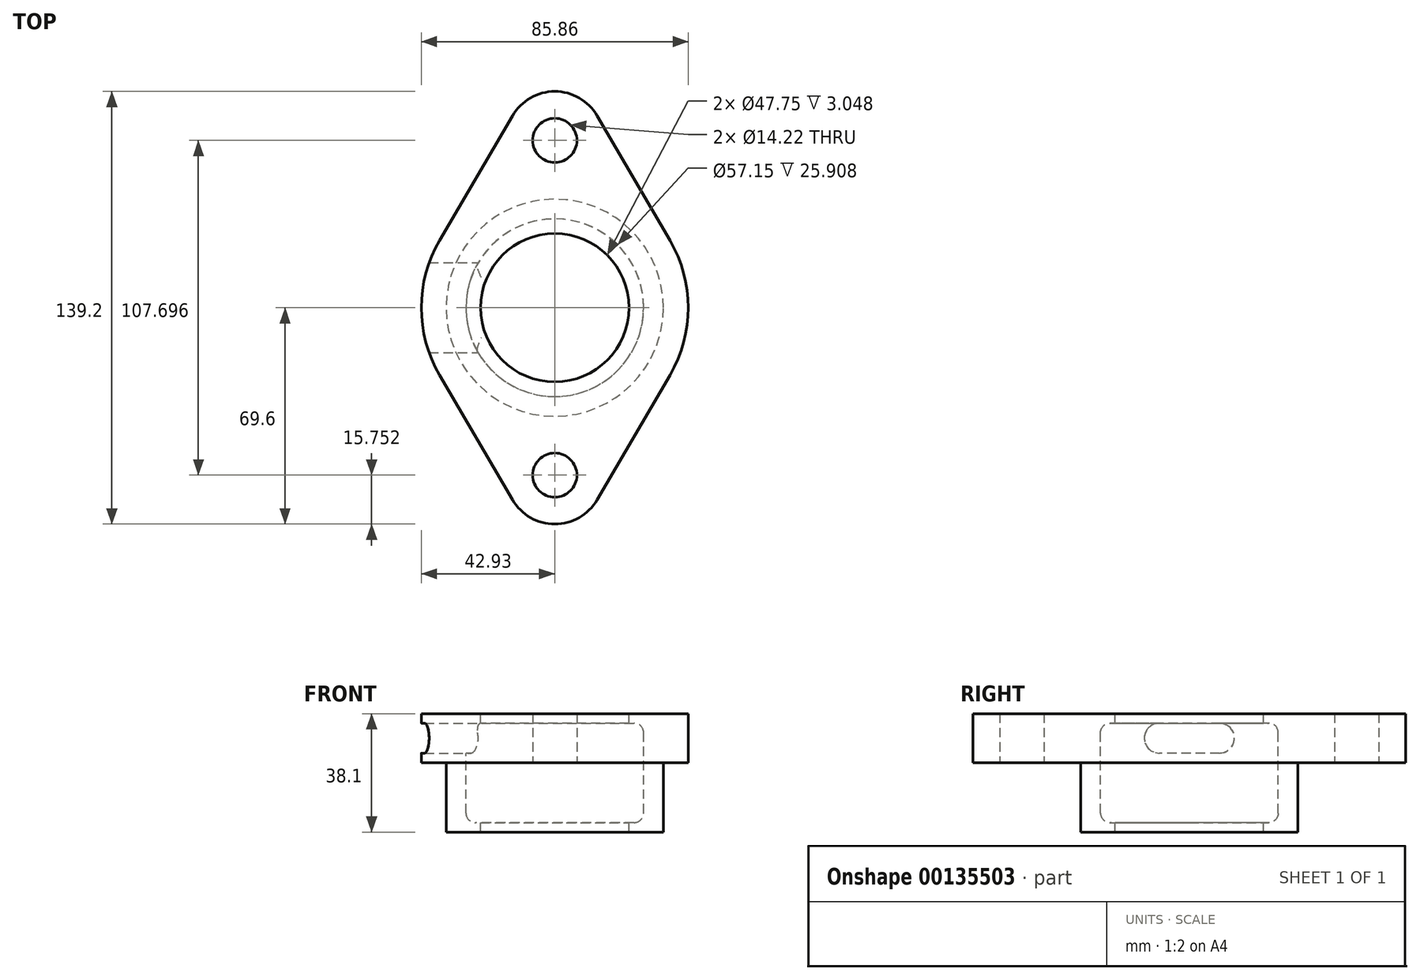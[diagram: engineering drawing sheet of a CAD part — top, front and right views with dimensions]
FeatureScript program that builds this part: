
annotation { "Feature Type Name" : "Feature", "Feature Type Description" : "" }
export const myFeature = defineFeature(function(context is Context, id is Id, definition is map)
    precondition{}
    {
        {
            var Q0;
            Q0=qCreatedBy(makeId("Top.planeOp"),FACE);
            var sketch = newSketch(context, id + "F0", { "sketchPlane" : qUnion([Q0])});
            skArc(sketch, "E0", {"start": v(-37.06, 21.67) * mm, "mid": v(-42.93, 0) * mm, "end": v(-37.06, -21.67) * mm});
            skLineSegment(sketch, "E1", {"start": v(0, 0) * mm, "end": v(0, 53.85) * mm, "construction": true});
            skLineSegment(sketch, "E2", {"start": v(0, 0) * mm, "end": v(0, -53.85) * mm, "construction": true});
            skCircle(sketch, "E3", {"center": v(0, 53.85) * mm, "radius": 7.11 * mm});
            skCircle(sketch, "E4", {"center": v(0, -53.85) * mm, "radius": 7.11 * mm});
            skArc(sketch, "E5", {"start": v(13.6, 61.8) * mm, "mid": v(0, 69.6) * mm, "end": v(-13.6, 61.8) * mm});
            skArc(sketch, "E6", {"start": v(-13.6, -61.8) * mm, "mid": v(0, -69.6) * mm, "end": v(13.6, -61.8) * mm});
            skLineSegment(sketch, "E7", {"start": v(-37.06, 21.67) * mm, "end": v(-13.6, 61.8) * mm});
            skLineSegment(sketch, "E8", {"start": v(13.6, 61.8) * mm, "end": v(37.06, 21.67) * mm});
            skLineSegment(sketch, "E9", {"start": v(37.06, -21.67) * mm, "end": v(13.6, -61.8) * mm});
            skLineSegment(sketch, "E10", {"start": v(-13.6, -61.8) * mm, "end": v(-37.06, -21.67) * mm});
            skArc(sketch, "E11.trimOffspring", {"start": v(37.06, -21.67) * mm, "mid": v(42.93, 0) * mm, "end": v(37.06, 21.67) * mm});
            skSolve(sketch);
        }
        {
            var Q0;
            Q0 = qSketchRegion(id + "F0", true);
            extrude(context, id + "F1", {"entities" : qUnion([Q0]), "depth" : 15.75 * mm});
        }
        {
            var Q0;
            Q0=makeQuery(id+"F1.opExtrude","CAP_FACE",FACE,{"disambiguationData":[OSD([sQuery(id+"F0.wireOp",EDGE,"E0"),sQuery(id+"F0.wireOp",EDGE,"E3"),sQuery(id+"F0.wireOp",EDGE,"E4"),sQuery(id+"F0.wireOp",EDGE,"E5"),sQuery(id+"F0.wireOp",EDGE,"E6"),sQuery(id+"F0.wireOp",EDGE,"E7"),sQuery(id+"F0.wireOp",EDGE,"E8"),sQuery(id+"F0.wireOp",EDGE,"E9"),sQuery(id+"F0.wireOp",EDGE,"E10"),sQuery(id+"F0.wireOp",EDGE,"E11.trimOffspring")])],"isStart":true});
            var sketch = newSketch(context, id + "F2", { "sketchPlane" : qUnion([Q0])});
            skCircle(sketch, "E12", {"center": v(0, 0) * mm, "radius": 34.93 * mm});
            skCircle(sketch, "E13", {"center": v(0, 0) * mm, "radius": 23.88 * mm});
            skSolve(sketch);
        }
        {
            var Q0;
            Q0 = qSketchRegion(id + "F2", true);
            extrude(context, id + "F3", {"entities" : qUnion([Q0]), "operationType" : NewBodyOperationType.ADD, "depth" : 22.35 * mm});
        }
        {
            var Q0;
            Q0=makeQuery(id+"F3.boolean.opBoolean","SPLIT",FACE,{"disambiguationData":[TD([makeQuery(id+"F3.opExtrude","SWEPT_FACE",FACE,{"disambiguationData":[OSD([sQuery(id+"F2.wireOp",EDGE,"E13")])]})])],"derivedFrom":makeQuery(id+"F1.opExtrude","CAP_FACE",FACE,{"disambiguationData":[OSD([sQuery(id+"F0.wireOp",EDGE,"E0"),sQuery(id+"F0.wireOp",EDGE,"E3"),sQuery(id+"F0.wireOp",EDGE,"E4"),sQuery(id+"F0.wireOp",EDGE,"E5"),sQuery(id+"F0.wireOp",EDGE,"E6"),sQuery(id+"F0.wireOp",EDGE,"E7"),sQuery(id+"F0.wireOp",EDGE,"E8"),sQuery(id+"F0.wireOp",EDGE,"E9"),sQuery(id+"F0.wireOp",EDGE,"E10"),sQuery(id+"F0.wireOp",EDGE,"E11.trimOffspring")])],"isStart":true})});
            extrude(context, id + "F4", {"entities" : qUnion([Q0]), "operationType" : NewBodyOperationType.REMOVE, "endBound" : BoundingType.THROUGH_ALL, "oppositeDirection" : true, "depth" : 25.4 * mm});
        }
        {
            var Q0;
            Q0=qCreatedBy(makeId("Front.planeOp"),FACE);
            var sketch = newSketch(context, id + "F5", { "sketchPlane" : qUnion([Q0])});
            skLineSegment(sketch, "E14", {"start": v(0, 0) * mm, "end": v(-28.58, 0) * mm, "construction": true});
            skLineSegment(sketch, "E15", {"start": v(-28.58, 0) * mm, "end": v(-28.58, 9.65) * mm});
            skLineSegment(sketch, "E16", {"start": v(-28.58, 0) * mm, "end": v(-28.58, -16.26) * mm});
            skLineSegment(sketch, "E17", {"start": v(-25.53, -19.3) * mm, "end": v(0, -19.3) * mm});
            skLineSegment(sketch, "E18", {"start": v(0, -19.3) * mm, "end": v(0, 12.7) * mm});
            skLineSegment(sketch, "E19", {"start": v(0, 12.7) * mm, "end": v(-25.53, 12.7) * mm});
            skPoint(sketch, "E20.visualSharp", {"position": v(-28.58, 12.7) * mm});
            skArc(sketch, "E20.filletArc", {"start": v(-25.53, 12.7) * mm, "mid": v(-27.68, 11.8) * mm, "end": v(-28.58, 9.65) * mm});
            skPoint(sketch, "E21.visualSharp", {"position": v(-28.58, -19.3) * mm});
            skArc(sketch, "E21.filletArc", {"start": v(-28.58, -16.26) * mm, "mid": v(-27.68, -18.41) * mm, "end": v(-25.53, -19.3) * mm});
            skSolve(sketch);
        }
        {
            var Q0;
            Q0 = qSketchRegion(id + "F5", true);
            var Q1;
            Q1=sQuery(id+"F5.wireOp",EDGE,"E18");
            revolve(context, id + "F6", {"operationType" : NewBodyOperationType.REMOVE, "entities" : qUnion([Q0]), "axis" : qUnion([Q1]), "revolveType" : RevolveType.FULL, "oppositeDirection" : true});
        }
        {
            var Q0;
            Q0=qCreatedBy(makeId("Right.planeOp"),FACE);
            var sketch = newSketch(context, id + "F7", { "sketchPlane" : qUnion([Q0])});
            skLineSegment(sketch, "E22", {"start": v(0, 0) * mm, "end": v(0, 7.87) * mm, "construction": true});
            skLineSegment(sketch, "E23", {"start": v(-9.65, 7.87) * mm, "end": v(9.65, 7.87) * mm, "construction": true});
            skArc(sketch, "E24", {"start": v(-9.65, 12.7) * mm, "mid": v(-14.48, 7.87) * mm, "end": v(-9.65, 3.05) * mm});
            skArc(sketch, "E25", {"start": v(9.65, 3.05) * mm, "mid": v(14.48, 7.87) * mm, "end": v(9.65, 12.7) * mm});
            skLineSegment(sketch, "E26", {"start": v(-9.65, 12.7) * mm, "end": v(9.65, 12.7) * mm});
            skLineSegment(sketch, "E27", {"start": v(9.65, 3.05) * mm, "end": v(-9.65, 3.05) * mm});
            skSolve(sketch);
        }
        {
            var Q0;
            Q0 = qSketchRegion(id + "F7", true);
            extrude(context, id + "F8", {"entities" : qUnion([Q0]), "operationType" : NewBodyOperationType.REMOVE, "endBound" : BoundingType.THROUGH_ALL, "oppositeDirection" : true, "depth" : 25.4 * mm});
        }
    });
